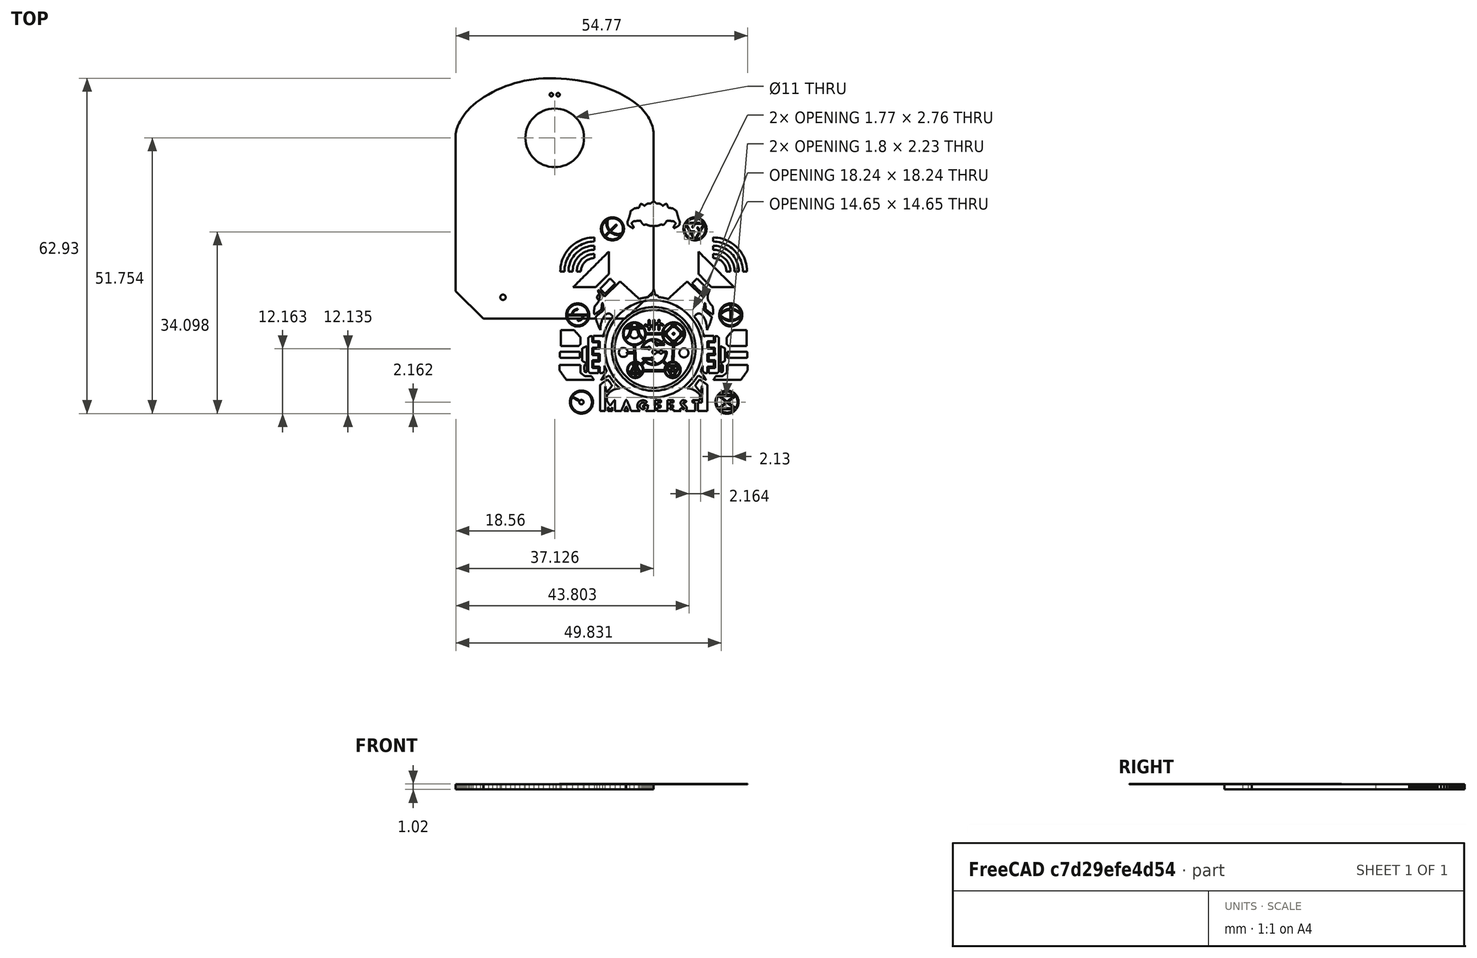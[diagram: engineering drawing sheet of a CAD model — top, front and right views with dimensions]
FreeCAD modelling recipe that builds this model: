
FCSTD DOCUMENT  (FreeCAD 0.19R24291 (Git))
Label: blade-plate-med-no-teeth
License: All rights reserved
LicenseURL: http://en.wikipedia.org/wiki/All_rights_reserved
objects: Part::Feature×106, Part::Extrusion×40, Part::MultiFuse×9, App::Part×5, PartDesign::CoordinateSystem×1, Sketcher::SketchObject×1
note: 157 computed .brp shape members not serialized (recipe doc carries the construction recipe); baked Part::Feature solids carry a one-line shape summary decoded from their .brp

FEATURE [PartDesign::CoordinateSystem] Local_CS_2f9
  AttacherType = Attacher::AttachEngine3D
FEATURE [Part::Feature] Pcb_2f9
  shape: bbox 37.12 x 45.09 x 1 mm, 78 faces (baked)
FEATURE [Sketcher::SketchObject] PCB_Sketch_2f9
  FullyConstrained = false
  sketch-geometry (72):
    g0: LineSegment StartX=18.2126 StartY=13.8473 StartZ=0 EndX=18.0682 EndY=14.2151 EndZ=0
    g1: LineSegment StartX=17.2906 StartY=15.6568 StartZ=0 EndX=17.0535 EndY=15.9973 EndZ=0
    g2: LineSegment StartX=17.7164 StartY=14.9469 StartZ=0 EndX=17.512 EndY=15.3058 EndZ=0
    g3: LineSegment StartX=18.4311 StartY=13.1203 StartZ=0 EndX=18.334 EndY=13.4816 EndZ=0
    g4: LineSegment StartX=17.9023 StartY=14.5825 StartZ=0 EndX=17.7164 EndY=14.9469 EndZ=0
    g5: LineSegment StartX=17.512 StartY=15.3058 StartZ=0 EndX=17.2906 EndY=15.6568 EndZ=0
    g6: LineSegment StartX=18.334 StartY=13.4816 StartZ=0 EndX=18.2126 EndY=13.8473 EndZ=0
    g7: LineSegment StartX=18.5022 StartY=12.7661 StartZ=0 EndX=18.4311 EndY=13.1203 EndZ=0
    g8: LineSegment StartX=18.0682 StartY=14.2151 StartZ=0 EndX=17.9023 EndY=14.5825 EndZ=0
    g9: LineSegment StartX=18.5609 StartY=12.0887 StartZ=0 EndX=18.546 EndY=12.4214 EndZ=0
    g10: LineSegment StartX=18.546 StartY=12.4214 StartZ=0 EndX=18.5022 EndY=12.7661 EndZ=0
    g11: LineSegment StartX=-1.00226 StartY=22.5449 StartZ=0 EndX=-2.16808 EndY=22.5134 EndZ=0
    g12: LineSegment StartX=-2.16808 StartY=22.5134 StartZ=0 EndX=-3.05347 EndY=22.4553 EndZ=0
    g13: LineSegment StartX=-3.05347 StartY=22.4553 StartZ=0 EndX=-3.94106 EndY=22.3603 EndZ=0
    g14: LineSegment StartX=-3.94106 StartY=22.3603 StartZ=0 EndX=-4.82869 EndY=22.2291 EndZ=0
    g15: LineSegment StartX=-4.82869 StartY=22.2291 StartZ=0 EndX=-5.71419 EndY=22.062 EndZ=0
    g16: LineSegment StartX=-5.71419 StartY=22.062 StartZ=0 EndX=-6.59539 EndY=21.8597 EndZ=0
    g17: LineSegment StartX=-6.59539 StartY=21.8597 StartZ=0 EndX=-7.47011 EndY=21.6227 EndZ=0
    g18: LineSegment StartX=-7.47011 StartY=21.6227 StartZ=0 EndX=-8.3362 EndY=21.3514 EndZ=0
    g19: LineSegment StartX=-8.3362 StartY=21.3514 StartZ=0 EndX=-9.19148 EndY=21.0464 EndZ=0
    g20: LineSegment StartX=-9.19148 StartY=21.0464 StartZ=0 EndX=-10.0338 EndY=20.7082 EndZ=0
    g21: LineSegment StartX=-10.0338 StartY=20.7082 StartZ=0 EndX=-10.8609 EndY=20.3374 EndZ=0
    g22: LineSegment StartX=-10.8609 StartY=20.3374 StartZ=0 EndX=-11.6708 EndY=19.9344 EndZ=0
    g23: LineSegment StartX=-11.6708 StartY=19.9344 StartZ=0 EndX=-12.4611 EndY=19.4999 EndZ=0
    g24: LineSegment StartX=-12.4611 StartY=19.4999 StartZ=0 EndX=-13.2298 EndY=19.0342 EndZ=0
    g25: LineSegment StartX=-13.2298 StartY=19.0342 StartZ=0 EndX=-13.9747 EndY=18.538 EndZ=0
    g26: LineSegment StartX=-13.9747 StartY=18.538 StartZ=0 EndX=-14.6936 EndY=18.0117 EndZ=0
    g27: LineSegment StartX=-14.6936 StartY=18.0117 StartZ=0 EndX=-15.3843 EndY=17.4559 EndZ=0
    g28: LineSegment StartX=-15.3843 StartY=17.4559 StartZ=0 EndX=-15.6818 EndY=17.19 EndZ=0
    g29: LineSegment StartX=-15.6818 StartY=17.19 StartZ=0 EndX=-15.9769 EndY=16.8978 EndZ=0
    g30: LineSegment StartX=-15.9769 StartY=16.8978 StartZ=0 EndX=-16.2674 EndY=16.5829 EndZ=0
    g31: LineSegment StartX=-16.2674 StartY=16.5829 StartZ=0 EndX=-16.5509 EndY=16.2489 EndZ=0
    g32: LineSegment StartX=-16.5509 StartY=16.2489 StartZ=0 EndX=-16.8251 EndY=15.8995 EndZ=0
    g33: LineSegment StartX=-16.8251 StartY=15.8995 StartZ=0 EndX=-17.0876 EndY=15.5384 EndZ=0
    g34: LineSegment StartX=-17.0876 StartY=15.5384 StartZ=0 EndX=-17.3361 EndY=15.1692 EndZ=0
    g35: LineSegment StartX=-17.3361 StartY=15.1692 StartZ=0 EndX=-17.5684 EndY=14.7956 EndZ=0
    g36: LineSegment StartX=-17.5684 StartY=14.7956 StartZ=0 EndX=-17.782 EndY=14.4213 EndZ=0
    g37: LineSegment StartX=-17.782 StartY=14.4213 StartZ=0 EndX=-17.9747 EndY=14.0499 EndZ=0
    g38: LineSegment StartX=-17.9747 StartY=14.0499 StartZ=0 EndX=-18.1441 EndY=13.6851 EndZ=0
    g39: LineSegment StartX=-18.1441 StartY=13.6851 StartZ=0 EndX=-18.2879 EndY=13.3306 EndZ=0
    g40: LineSegment StartX=-18.2879 StartY=13.3306 StartZ=0 EndX=-18.4039 EndY=12.9901 EndZ=0
    g41: LineSegment StartX=-18.4039 StartY=12.9901 StartZ=0 EndX=-18.4895 EndY=12.6671 EndZ=0
    g42: LineSegment StartX=-18.4895 StartY=12.6671 StartZ=0 EndX=-18.5426 EndY=12.3655 EndZ=0
    g43: LineSegment StartX=-18.5426 StartY=12.3655 StartZ=0 EndX=-18.5609 EndY=12.0887 EndZ=0
    g44: LineSegment StartX=-18.5609 StartY=12.0887 StartZ=0 EndX=-18.5609 EndY=-17.3932 EndZ=0
    g45: LineSegment StartX=-18.5609 StartY=-17.3932 StartZ=0 EndX=-13.4077 EndY=-22.5463 EndZ=0
    g46: LineSegment StartX=-13.4077 StartY=-22.5463 StartZ=0 EndX=13.4015 EndY=-22.5463 EndZ=0
    g47: LineSegment StartX=13.4015 StartY=-22.5463 StartZ=0 EndX=18.5609 EndY=-17.387 EndZ=0
    g48: LineSegment StartX=18.5609 StartY=-17.387 StartZ=0 EndX=18.5609 EndY=12.0887 EndZ=0
    g49: LineSegment StartX=17.0535 StartY=15.9973 StartZ=0 EndX=16.8024 EndY=16.3249 EndZ=0
    g50: LineSegment StartX=16.8024 StartY=16.3249 StartZ=0 EndX=16.5386 EndY=16.637 EndZ=0
    g51: LineSegment StartX=16.5386 StartY=16.637 StartZ=0 EndX=16.2636 EndY=16.9312 EndZ=0
    g52: LineSegment StartX=16.2636 StartY=16.9312 StartZ=0 EndX=15.979 EndY=17.205 EndZ=0
    g53: LineSegment StartX=15.979 StartY=17.205 StartZ=0 EndX=15.6861 EndY=17.4559 EndZ=0
    g54: LineSegment StartX=15.6861 StartY=17.4559 StartZ=0 EndX=14.8776 EndY=18.0704 EndZ=0
    g55: LineSegment StartX=14.8776 StartY=18.0704 StartZ=0 EndX=14.0352 EndY=18.6422 EndZ=0
    g56: LineSegment StartX=14.0352 StartY=18.6422 StartZ=0 EndX=13.1617 EndY=19.1719 EndZ=0
    g57: LineSegment StartX=13.1617 StartY=19.1719 StartZ=0 EndX=12.2595 EndY=19.6602 EndZ=0
    g58: LineSegment StartX=12.2595 StartY=19.6602 StartZ=0 EndX=11.3315 EndY=20.1077 EndZ=0
    g59: LineSegment StartX=11.3315 StartY=20.1077 StartZ=0 EndX=10.3802 EndY=20.5152 EndZ=0
    g60: LineSegment StartX=10.3802 StartY=20.5152 StartZ=0 EndX=9.40835 EndY=20.8832 EndZ=0
    g61: LineSegment StartX=9.40835 StartY=20.8832 StartZ=0 EndX=8.4186 EndY=21.2126 EndZ=0
    g62: LineSegment StartX=8.4186 StartY=21.2126 StartZ=0 EndX=7.41361 EndY=21.5039 EndZ=0
    g63: LineSegment StartX=7.41361 StartY=21.5039 StartZ=0 EndX=6.39603 EndY=21.7579 EndZ=0
    g64: LineSegment StartX=6.39603 StartY=21.7579 StartZ=0 EndX=5.36853 EndY=21.9751 EndZ=0
    g65: LineSegment StartX=5.36853 StartY=21.9751 StartZ=0 EndX=4.33378 EndY=22.1563 EndZ=0
    g66: LineSegment StartX=4.33378 StartY=22.1563 StartZ=0 EndX=3.29443 EndY=22.3022 EndZ=0
    g67: LineSegment StartX=3.29443 StartY=22.3022 StartZ=0 EndX=2.25315 EndY=22.4135 EndZ=0
    g68: LineSegment StartX=2.25315 StartY=22.4135 StartZ=0 EndX=1.2126 EndY=22.4907 EndZ=0
    g69: LineSegment StartX=1.2126 StartY=22.4907 StartZ=0 EndX=0.175441 EndY=22.5346 EndZ=0
    g70: LineSegment StartX=0.175441 StartY=22.5346 StartZ=0 EndX=-1.00226 EndY=22.5449 EndZ=0
    g71: Circle CenterX=0 CenterY=11.3637 CenterZ=0 NormalX=0 NormalY=0 NormalZ=1 AngleXU=0 Radius=5.5
  constraints (71):
    c: Coincident(g45,g44)
    c: Coincident(g43,g44)
    c: Coincident(g43,g42)
    c: Coincident(g42,g41)
    c: Coincident(g41,g40)
    c: Coincident(g40,g39)
    c: Coincident(g39,g38)
    c: Coincident(g38,g37)
    c: Coincident(g37,g36)
    c: Coincident(g36,g35)
    c: Coincident(g35,g34)
    c: Coincident(g34,g33)
    c: Coincident(g32,g33)
    c: Coincident(g32,g31)
    c: Coincident(g30,g31)
    c: Coincident(g29,g30)
    c: Coincident(g28,g29)
    c: Coincident(g27,g28)
    c: Coincident(g27,g26)
    c: Coincident(g25,g26)
    c: Coincident(g46,g45)
    c: Coincident(g24,g25)
    c: Coincident(g24,g23)
    c: Coincident(g23,g22)
    c: Coincident(g22,g21)
    c: Coincident(g20,g21)
    c: Coincident(g19,g20)
    c: Coincident(g18,g19)
    c: Coincident(g17,g18)
    c: Coincident(g17,g16)
    c: Coincident(g16,g15)
    c: Coincident(g15,g14)
    c: Coincident(g14,g13)
    c: Coincident(g13,g12)
    c: Coincident(g12,g11)
    c: Coincident(g11,g70)
    c: Coincident(g70,g69)
    c: Coincident(g68,g69)
    c: Coincident(g67,g68)
    c: Coincident(g66,g67)
    c: Coincident(g65,g66)
    c: Coincident(g65,g64)
    c: Coincident(g63,g64)
    c: Coincident(g62,g63)
    c: Coincident(g62,g61)
    c: Coincident(g60,g61)
    c: Coincident(g60,g59)
    c: Coincident(g59,g58)
    c: Coincident(g58,g57)
    c: Coincident(g56,g57)
    c: Coincident(g46,g47)
    c: Coincident(g55,g56)
    c: Coincident(g55,g54)
    c: Coincident(g54,g53)
    c: Coincident(g52,g53)
    c: Coincident(g51,g52)
    c: Coincident(g51,g50)
    c: Coincident(g49,g50)
    c: Coincident(g1,g49)
    c: Coincident(g1,g5)
    c: Coincident(g5,g2)
    c: Coincident(g4,g2)
    c: Coincident(g8,g4)
    c: Coincident(g0,g8)
    c: Coincident(g0,g6)
    c: Coincident(g6,g3)
    c: Coincident(g3,g7)
    c: Coincident(g10,g7)
    c: Coincident(g10,g9)
    c: Coincident(g48,g47)
    c: Coincident(g48,g9)
FEATURE [App::Part] Board_Geoms_2f9
  Group = -> [Local_CS_2f9,Pcb_2f9,PCB_Sketch_2f9]
  Origin = -> Origin
FEATURE [App::Part] Step_Models_2f9
  Origin = -> Origin002
FEATURE [App::Part] Board_2f9  label="blade-plate-med-no-teeth"
  Group = -> [Board_Geoms_2f9,Step_Models_2f9]
  Origin = -> Origin001
FEATURE [Part::Feature] path950
  shape: bbox 6.431 x 2.806 x 2e-07 mm, 0 faces, 0 solids (baked)
FEATURE [Part::Feature] path952
  shape: bbox 2.242 x 5.916 x 2e-07 mm, 0 faces, 0 solids (baked)
FEATURE [Part::Feature] path948
  shape: bbox 6.431 x 2.806 x 2e-07 mm, 0 faces, 0 solids (baked)
FEATURE [Part::Feature] path946
  shape: bbox 0.4955 x 1.452 x 2e-07 mm, 0 faces, 0 solids (baked)
FEATURE [Part::Feature] path942
  shape: bbox 3.739 x 1.126 x 2e-07 mm, 0 faces, 0 solids (baked)
FEATURE [Part::Feature] path938
  shape: bbox 0.8516 x 3.223 x 2e-07 mm, 0 faces, 0 solids (baked)
FEATURE [Part::Feature] path936
  shape: bbox 0.8516 x 3.223 x 2e-07 mm, 0 faces, 0 solids (baked)
FEATURE [Part::Feature] path934
  shape: bbox 1.909 x 6.981 x 2e-07 mm, 0 faces, 0 solids (baked)
FEATURE [Part::Feature] path932
  shape: bbox 1.909 x 6.981 x 2e-07 mm, 0 faces, 0 solids (baked)
FEATURE [Part::Feature] path940
  shape: bbox 3.739 x 1.126 x 2e-07 mm, 0 faces, 0 solids (baked)
FEATURE [Part::Feature] path930
  shape: bbox 3.738 x 2.965 x 2e-07 mm, 0 faces, 0 solids (baked)
FEATURE [Part::Feature] path928
  shape: bbox 3.738 x 2.965 x 2e-07 mm, 0 faces, 0 solids (baked)
FEATURE [Part::Feature] path944
  shape: bbox 0.4954 x 1.452 x 2e-07 mm, 0 faces, 0 solids (baked)
FEATURE [Part::Feature] path954
  shape: bbox 2.232 x 5.914 x 2e-07 mm, 0 faces, 0 solids (baked)
FEATURE [Part::Feature] path958
  shape: bbox 0.8191 x 0.724 x 2e-07 mm, 0 faces, 0 solids (baked)
FEATURE [Part::Feature] path956
  shape: bbox 0.8346 x 0.8904 x 2e-07 mm, 0 faces, 0 solids (baked)
FEATURE [Part::Feature] path926
  shape: bbox 14.65 x 14.65 x 2e-07 mm, 0 faces, 0 solids (baked)
FEATURE [Part::Feature] path920
  shape: bbox 2.839 x 2.838 x 2e-07 mm, 0 faces, 0 solids (baked)
FEATURE [Part::Feature] path904
  shape: bbox 6.368 x 6.368 x 2e-07 mm, 0 faces, 0 solids (baked)
FEATURE [Part::Feature] path906
  shape: bbox 4.82 x 4.82 x 2e-07 mm, 0 faces, 0 solids (baked)
FEATURE [Part::Feature] path918
  shape: bbox 2.838 x 2.838 x 2e-07 mm, 0 faces, 0 solids (baked)
FEATURE [Part::Feature] path924
  shape: bbox 18.24 x 18.24 x 2e-07 mm, 0 faces, 0 solids (baked)
FEATURE [Part::Feature] path908
  shape: bbox 4.82 x 4.82 x 2e-07 mm, 0 faces, 0 solids (baked)
FEATURE [Part::Feature] path916
  shape: bbox 3.272 x 3.272 x 2e-07 mm, 0 faces, 0 solids (baked)
FEATURE [Part::Feature] path912
  shape: bbox 6.702 x 6.691 x 2e-07 mm, 0 faces, 0 solids (baked)
FEATURE [Part::Feature] path857_8_0_9
  shape: bbox 9.846 x 4.976 x 2e-07 mm, 0 faces, 0 solids (baked)
FEATURE [Part::Feature] path914
  shape: bbox 3.272 x 3.272 x 2e-07 mm, 0 faces, 0 solids (baked)
FEATURE [Part::Feature] path902
  shape: bbox 6.368 x 6.368 x 2e-07 mm, 0 faces, 0 solids (baked)
FEATURE [Part::Feature] path922
  shape: bbox 22.57 x 24.3 x 2e-07 mm, 0 faces, 0 solids (baked)
FEATURE [Part::MultiFuse] Fusion
  Shapes = -> [path924,path922]
FEATURE [Part::Feature] path910
  shape: bbox 6.702 x 6.691 x 2e-07 mm, 0 faces, 0 solids (baked)
FEATURE [Part::Extrusion] Extrude036
  Base = -> path944
  Dir = (0,0,1)
  DirMode = 0
  FaceMakerClass = Part::FaceMakerBullseye
  LengthFwd = 0.01
  LengthRev = 0
  Solid = true
  Symmetric = false
FEATURE [Part::Extrusion] Extrude039
  Base = -> path938
  Dir = (0,0,1)
  DirMode = 0
  FaceMakerClass = Part::FaceMakerBullseye
  LengthFwd = 0.01
  LengthRev = 0
  Solid = true
  Symmetric = false
FEATURE [Part::Extrusion] Extrude041
  Base = -> path934
  Dir = (0,0,1)
  DirMode = 0
  FaceMakerClass = Part::FaceMakerBullseye
  LengthFwd = 0.01
  LengthRev = 0
  Solid = true
  Symmetric = false
FEATURE [Part::Extrusion] Extrude042
  Base = -> path932
  Dir = (0,0,1)
  DirMode = 0
  FaceMakerClass = Part::FaceMakerBullseye
  LengthFwd = 0.01
  LengthRev = 0
  Solid = true
  Symmetric = false
FEATURE [Part::Extrusion] Extrude040
  Base = -> path936
  Dir = (0,0,1)
  DirMode = 0
  FaceMakerClass = Part::FaceMakerBullseye
  LengthFwd = 0.01
  LengthRev = 0
  Solid = true
  Symmetric = false
FEATURE [Part::Extrusion] Extrude043
  Base = -> path930
  Dir = (0,0,1)
  DirMode = 0
  FaceMakerClass = Part::FaceMakerBullseye
  LengthFwd = 0.01
  LengthRev = 0
  Solid = true
  Symmetric = false
FEATURE [Part::Extrusion] Extrude029
  Base = -> path958
  Dir = (0,0,1)
  DirMode = 0
  FaceMakerClass = Part::FaceMakerBullseye
  LengthFwd = 0.01
  LengthRev = 0
  Solid = true
  Symmetric = false
FEATURE [Part::Extrusion] Extrude030
  Base = -> path956
  Dir = (0,0,1)
  DirMode = 0
  FaceMakerClass = Part::FaceMakerBullseye
  LengthFwd = 0.01
  LengthRev = 0
  Solid = true
  Symmetric = false
FEATURE [Part::Extrusion] Extrude034
  Base = -> path948
  Dir = (0,0,1)
  DirMode = 0
  FaceMakerClass = Part::FaceMakerBullseye
  LengthFwd = 0.01
  LengthRev = 0
  Solid = true
  Symmetric = false
FEATURE [Part::Extrusion] Extrude035
  Base = -> path946
  Dir = (0,0,1)
  DirMode = 0
  FaceMakerClass = Part::FaceMakerBullseye
  LengthFwd = 0.01
  LengthRev = 0
  Solid = true
  Symmetric = false
FEATURE [Part::Extrusion] Extrude038
  Base = -> path940
  Dir = (0,0,1)
  DirMode = 0
  FaceMakerClass = Part::FaceMakerBullseye
  LengthFwd = 0.01
  LengthRev = 0
  Solid = true
  Symmetric = false
FEATURE [Part::Extrusion] Extrude032
  Base = -> path952
  Dir = (0,0,1)
  DirMode = 0
  FaceMakerClass = Part::FaceMakerBullseye
  LengthFwd = 0.01
  LengthRev = 0
  Solid = true
  Symmetric = false
FEATURE [Part::Extrusion] Extrude066
  Base = -> path942
  Dir = (0,0,1)
  DirMode = 0
  FaceMakerClass = Part::FaceMakerBullseye
  LengthFwd = 0.01
  LengthRev = 0
  Solid = true
  Symmetric = false
FEATURE [Part::Extrusion] Extrude046
  Base = -> path920
  Dir = (0,0,1)
  DirMode = 0
  FaceMakerClass = Part::FaceMakerBullseye
  LengthFwd = 0.01
  LengthRev = 0
  Solid = true
  Symmetric = false
FEATURE [Part::Extrusion] Extrude062
  Base = -> path950
  Dir = (0,0,1)
  DirMode = 0
  FaceMakerClass = Part::FaceMakerBullseye
  LengthFwd = 0.01
  LengthRev = 0
  Solid = true
  Symmetric = false
FEATURE [Part::Extrusion] Extrude076
  Base = -> path918
  Dir = (0,0,1)
  DirMode = 0
  FaceMakerClass = Part::FaceMakerBullseye
  LengthFwd = 0.01
  LengthRev = 0
  Solid = true
  Symmetric = false
FEATURE [Part::Extrusion] Extrude050
  Base = -> path912
  Dir = (0,0,1)
  DirMode = 0
  FaceMakerClass = Part::FaceMakerBullseye
  LengthFwd = 0.01
  LengthRev = 0
  Solid = true
  Symmetric = false
FEATURE [Part::Extrusion] Extrude048
  Base = -> path916
  Dir = (0,0,1)
  DirMode = 0
  FaceMakerClass = Part::FaceMakerBullseye
  LengthFwd = 0.01
  LengthRev = 0
  Solid = true
  Symmetric = false
FEATURE [Part::Extrusion] Extrude045
  Base = -> path926
  Dir = (0,0,1)
  DirMode = 0
  FaceMakerClass = Part::FaceMakerBullseye
  LengthFwd = 0.01
  LengthRev = 0
  Solid = true
  Symmetric = false
FEATURE [Part::Extrusion] Extrude049
  Base = -> path914
  Dir = (0,0,1)
  DirMode = 0
  FaceMakerClass = Part::FaceMakerBullseye
  LengthFwd = 0.01
  LengthRev = 0
  Solid = true
  Symmetric = false
FEATURE [Part::Extrusion] Extrude051
  Base = -> path910
  Dir = (0,0,1)
  DirMode = 0
  FaceMakerClass = Part::FaceMakerBullseye
  LengthFwd = 0.01
  LengthRev = 0
  Solid = true
  Symmetric = false
FEATURE [Part::Extrusion] Extrude053
  Base = -> path906
  Dir = (0,0,1)
  DirMode = 0
  FaceMakerClass = Part::FaceMakerBullseye
  LengthFwd = 0.01
  LengthRev = 0
  Solid = true
  Symmetric = false
FEATURE [Part::Extrusion] Extrude055
  Base = -> path902
  Dir = (0,0,1)
  DirMode = 0
  FaceMakerClass = Part::FaceMakerBullseye
  LengthFwd = 0.01
  LengthRev = 0
  Solid = true
  Symmetric = false
FEATURE [Part::Extrusion] Extrude056
  Base = -> path857_8_0_9
  Dir = (0,0,1)
  DirMode = 0
  FaceMakerClass = Part::FaceMakerBullseye
  LengthFwd = 0.01
  LengthRev = 0
  Solid = true
  Symmetric = false
FEATURE [Part::Extrusion] Extrude057
  Base = -> Fusion
  Dir = (0,0,1)
  DirMode = 0
  FaceMakerClass = Part::FaceMakerBullseye
  LengthFwd = 0.01
  LengthRev = 0
  Solid = true
  Symmetric = false
FEATURE [Part::Extrusion] Extrude044
  Base = -> path928
  Dir = (0,0,1)
  DirMode = 0
  FaceMakerClass = Part::FaceMakerBullseye
  LengthFwd = 0.01
  LengthRev = 0
  Solid = true
  Symmetric = false
FEATURE [Part::Extrusion] Extrude083
  Base = -> path904
  Dir = (0,0,1)
  DirMode = 0
  FaceMakerClass = Part::FaceMakerBullseye
  LengthFwd = 0.01
  LengthRev = 0
  Solid = true
  Symmetric = false
FEATURE [Part::Extrusion] Extrude081
  Base = -> path908
  Dir = (0,0,1)
  DirMode = 0
  FaceMakerClass = Part::FaceMakerBullseye
  LengthFwd = 0.01
  LengthRev = 0
  Solid = true
  Symmetric = false
FEATURE [Part::Feature] path7669_6_9_7_1_4
  shape: bbox 4.579 x 2.816 x 2e-07 mm, 1 faces, 0 solids (baked)
FEATURE [Part::Feature] path959_74_5_9
  shape: bbox 1.157 x 1.157 x 2e-07 mm, 1 faces, 0 solids (baked)
FEATURE [Part::Feature] path1142_5_3
  shape: bbox 1.86 x 1.86 x 2e-07 mm, 1 faces, 0 solids (baked)
FEATURE [Part::Feature] path1139_8_8
  shape: bbox 1.86 x 1.86 x 2e-07 mm, 1 faces, 0 solids (baked)
FEATURE [Part::Feature] path959_7_3_0_1
  shape: bbox 1.157 x 1.157 x 2e-07 mm, 1 faces, 0 solids (baked)
FEATURE [Part::Feature] path959_7_34_5
  shape: bbox 1.157 x 1.157 x 2e-07 mm, 1 faces, 0 solids (baked)
FEATURE [Part::Feature] rect1059_6_6
  shape: bbox 1.86 x 1.86 x 2e-07 mm, 1 faces, 0 solids (baked)
FEATURE [Part::Feature] rect1081_4_5_7
  shape: bbox 2.152 x 4.303 x 2e-07 mm, 1 faces, 0 solids (baked)
FEATURE [Part::Feature] rect1081_5_0_2
  shape: bbox 2.152 x 4.303 x 2e-07 mm, 1 faces, 0 solids (baked)
FEATURE [Part::Feature] rect1081_4_0_1_9
  shape: bbox 2.152 x 4.303 x 2e-07 mm, 1 faces, 0 solids (baked)
FEATURE [Part::Feature] path1849_7_9
  Placement = pos=(-72.7848,130.054,0) rot=(0,0,1;0rad)
  shape: bbox 1.711 x 1.711 x 2e-07 mm, 1 faces, 0 solids (baked)
FEATURE [Part::Feature] rect1857_9_3
  shape: bbox 3.613 x 0.2543 x 2e-07 mm, 1 faces, 0 solids (baked)
FEATURE [Part::Feature] path959_3_7
  shape: bbox 1.157 x 1.157 x 2e-07 mm, 1 faces, 0 solids (baked)
FEATURE [Part::Feature] rect1081_3_2
  shape: bbox 2.152 x 4.303 x 2e-07 mm, 1 faces, 0 solids (baked)
FEATURE [Part::Feature] path1108_9_5
  shape: bbox 1.86 x 1.86 x 2e-07 mm, 1 faces, 0 solids (baked)
FEATURE [Part::Feature] path7669_6_9_6_5
  shape: bbox 4.395 x 1.945 x 2e-07 mm, 1 faces, 0 solids (baked)
FEATURE [Part::Feature] path1387
  shape: bbox 2.857 x 0.6324 x 2e-07 mm, 0 faces, 0 solids (baked)
FEATURE [Part::Feature] path1401
  shape: bbox 3.191 x 0.8343 x 2e-07 mm, 0 faces, 0 solids (baked)
FEATURE [Part::Feature] path1415
  shape: bbox 2.983 x 1.481 x 2e-07 mm, 0 faces, 0 solids (baked)
FEATURE [Part::Feature] path1265
  shape: bbox 4.525 x 4.463 x 2e-07 mm, 0 faces, 0 solids (baked)
FEATURE [Part::Feature] path1405
  shape: bbox 1.856 x 2.763 x 2e-07 mm, 0 faces, 0 solids (baked)
FEATURE [Part::Feature] path1297
  shape: bbox 4.563 x 4.468 x 2e-07 mm, 0 faces, 0 solids (baked)
FEATURE [Part::Feature] path1407
  shape: bbox 1.805 x 2.762 x 2e-07 mm, 0 faces, 0 solids (baked)
FEATURE [Part::Feature] path1403
  shape: bbox 3.293 x 2.849 x 2e-07 mm, 0 faces, 0 solids (baked)
FEATURE [Part::Feature] path1253
  shape: bbox 4.564 x 4.449 x 2e-07 mm, 0 faces, 0 solids (baked)
FEATURE [Part::Feature] path1413
  shape: bbox 1.481 x 2.981 x 2e-07 mm, 0 faces, 0 solids (baked)
FEATURE [Part::Feature] path1411
  shape: bbox 3.034 x 2.972 x 2e-07 mm, 0 faces, 0 solids (baked)
FEATURE [Part::Feature] path1389
  shape: bbox 2.672 x 1.025 x 2e-07 mm, 0 faces, 0 solids (baked)
FEATURE [Part::Feature] rect1270_8_2_80
  shape: bbox 0.4357 x 3.344 x 2e-07 mm, 1 faces, 0 solids (baked)
FEATURE [Part::Feature] path2766_2_6
  shape: bbox 1.318 x 2.285 x 2e-07 mm, 1 faces, 0 solids (baked)
FEATURE [Part::Feature] path2577_5_9
  shape: bbox 1.312 x 2.285 x 2e-07 mm, 1 faces, 0 solids (baked)
FEATURE [Part::Feature] path2376_2_1_7_1_5_5
  shape: bbox 0.9033 x 0.9033 x 2e-07 mm, 1 faces, 0 solids (baked)
FEATURE [Part::Feature] path2536_4_8_8
  shape: bbox 0.5554 x 0.5554 x 2e-07 mm, 1 faces, 0 solids (baked)
FEATURE [Part::Feature] path2536_7_2_0
  shape: bbox 0.5554 x 0.5554 x 2e-07 mm, 1 faces, 0 solids (baked)
FEATURE [Part::Feature] rect1270_3
  shape: bbox 3.165 x 0.2677 x 2e-07 mm, 1 faces, 0 solids (baked)
FEATURE [Part::Feature] rect1270_8_2_8_0
  shape: bbox 0.4357 x 3.344 x 2e-07 mm, 1 faces, 0 solids (baked)
FEATURE [Part::Feature] path2376_0
  shape: bbox 1.713 x 1.713 x 2e-07 mm, 0 faces, 0 solids (baked)
FEATURE [Part::Extrusion] Extrude088
  Base = -> path2376_0
  Dir = (0,0,1)
  DirMode = 0
  FaceMakerClass = Part::FaceMakerBullseye
  LengthFwd = 0.02
  LengthRev = 0
  Solid = true
  Symmetric = false
FEATURE [Part::Feature] rect2443_9_0
  shape: bbox 0.1757 x 2.045 x 2e-07 mm, 1 faces, 0 solids (baked)
FEATURE [Part::Feature] path1277
  shape: bbox 4.563 x 4.468 x 2e-07 mm, 0 faces, 0 solids (baked)
FEATURE [Part::Feature] path2536_8_1
  shape: bbox 0.5554 x 0.5554 x 2e-07 mm, 1 faces, 0 solids (baked)
FEATURE [Part::Feature] path1489_8_2
  shape: bbox 0.942 x 0.942 x 2e-07 mm, 1 faces, 0 solids (baked)
FEATURE [Part::Feature] path1875_9_6
  shape: bbox 1.46 x 3.14 x 2e-07 mm, 1 faces, 0 solids (baked)
FEATURE [Part::Feature] path1875_0_1_3
  shape: bbox 1.46 x 3.14 x 2e-07 mm, 1 faces, 0 solids (baked)
FEATURE [Part::Feature] path2088_1_1_1
  shape: bbox 1.531 x 3.062 x 2e-07 mm, 1 faces, 0 solids (baked)
FEATURE [Part::Feature] path2118_4_2_1
  shape: bbox 1.532 x 3.062 x 2e-07 mm, 1 faces, 0 solids (baked)
FEATURE [Part::Feature] rect1270_8_5_2
  shape: bbox 1.5 x 0.2677 x 2e-07 mm, 1 faces, 0 solids (baked)
FEATURE [Part::Feature] path1377
  shape: bbox 3.891 x 1.793 x 2e-07 mm, 0 faces, 0 solids (baked)
FEATURE [Part::Feature] path1371
  shape: bbox 1.847 x 1.688 x 2e-07 mm, 0 faces, 0 solids (baked)
FEATURE [Part::Feature] path2376_2_1_6_8_8
  Placement = pos=(-74.8536,126.557,0) rot=(0,0,1;0rad)
  shape: bbox 1.713 x 1.713 x 2e-07 mm, 1 faces, 0 solids (baked)
FEATURE [Part::Feature] path8031_8
  shape: bbox 3.53 x 1.981 x 2e-07 mm, 0 faces, 0 solids (baked)
FEATURE [Part::Extrusion] Extrude091
  Base = -> path8031_8
  Dir = (0,0,1)
  DirMode = 0
  FaceMakerClass = Part::FaceMakerBullseye
  LengthFwd = 0.02
  LengthRev = 0
  Solid = true
  Symmetric = false
FEATURE [Part::Feature] path1383
  shape: bbox 3.925 x 1.972 x 2e-07 mm, 0 faces, 0 solids (baked)
FEATURE [Part::Feature] path2376_2_1_7_1_48_8_4_2
  shape: bbox 0.7776 x 0.7776 x 2e-07 mm, 1 faces, 0 solids (baked)
FEATURE [Part::Feature] path10299_4
  shape: bbox 0.3689 x 0.3694 x 2e-07 mm, 0 faces, 0 solids (baked)
FEATURE [Part::Extrusion] Extrude089
  Base = -> path10299_4
  Dir = (0,0,1)
  DirMode = 0
  FaceMakerClass = Part::FaceMakerBullseye
  LengthFwd = 0.02
  LengthRev = 0
  Solid = true
  Symmetric = false
FEATURE [Part::Feature] path1381
  shape: bbox 3.926 x 1.869 x 2e-07 mm, 0 faces, 0 solids (baked)
FEATURE [Part::Feature] path2376_2_1_7_1_48_89_5
  shape: bbox 0.7776 x 0.7776 x 2e-07 mm, 1 faces, 0 solids (baked)
FEATURE [Part::Feature] path1369
  shape: bbox 1.846 x 1.684 x 2e-07 mm, 0 faces, 0 solids (baked)
FEATURE [Part::Feature] path1489_6
  shape: bbox 0.942 x 0.942 x 2e-07 mm, 1 faces, 0 solids (baked)
FEATURE [Part::Feature] path1373
  shape: bbox 1.836 x 1.915 x 2e-07 mm, 0 faces, 0 solids (baked)
FEATURE [Part::Feature] rect1270_8_6
  shape: bbox 4.112 x 0.2677 x 2e-07 mm, 1 faces, 0 solids (baked)
FEATURE [Part::Feature] path1273
  shape: bbox 4.563 x 4.468 x 2e-07 mm, 0 faces, 0 solids (baked)
FEATURE [Part::Feature] path1269
  shape: bbox 4.563 x 4.451 x 2e-07 mm, 0 faces, 0 solids (baked)
FEATURE [Part::Feature] path2118_5_5_5
  shape: bbox 1.532 x 3.062 x 2e-07 mm, 1 faces, 0 solids (baked)
FEATURE [Part::Feature] path1397
  shape: bbox 2.871 x 0.6613 x 2e-07 mm, 0 faces, 0 solids (baked)
FEATURE [Part::Feature] path1395
  shape: bbox 2.655 x 1.019 x 2e-07 mm, 0 faces, 0 solids (baked)
FEATURE [Part::Feature] path1393
  shape: bbox 1.826 x 2.23 x 2e-07 mm, 0 faces, 0 solids (baked)
FEATURE [Part::Feature] path1391
  shape: bbox 1.826 x 2.231 x 2e-07 mm, 0 faces, 0 solids (baked)
FEATURE [Part::Feature] path1375
  shape: bbox 1.832 x 1.915 x 2e-07 mm, 0 faces, 0 solids (baked)
FEATURE [Part::Feature] path1365
  shape: bbox 4.136 x 4.058 x 2e-07 mm, 0 faces, 0 solids (baked)
FEATURE [Part::Feature] path2088_9_5_6
  shape: bbox 1.531 x 3.062 x 2e-07 mm, 1 faces, 0 solids (baked)
FEATURE [Part::Feature] path2182_0_4_3_8
  shape: bbox 1.211 x 2.1 x 2e-07 mm, 1 faces, 0 solids (baked)
FEATURE [Part::Feature] path2182_0_0_8
  shape: bbox 1.211 x 2.1 x 2e-07 mm, 1 faces, 0 solids (baked)
FEATURE [Part::Feature] rect1392_7_6_1
  shape: bbox 0.7492 x 0.7492 x 2e-07 mm, 1 faces, 0 solids (baked)
FEATURE [Part::Feature] rect1392_7_4
  shape: bbox 0.7492 x 0.7492 x 2e-07 mm, 1 faces, 0 solids (baked)
FEATURE [Part::Feature] path1427
  shape: bbox 14.65 x 14.65 x 2e-07 mm, 0 faces, 0 solids (baked)
FEATURE [Part::Feature] path8265_3
  shape: bbox 15.74 x 15.74 x 2e-07 mm, 0 faces, 0 solids (baked)
FEATURE [Part::MultiFuse] Fusion001
  Shapes = -> [path1365,path1277]
FEATURE [Part::Extrusion] Extrude087
  Base = -> Fusion001
  Dir = (0,0,1)
  DirMode = 0
  FaceMakerClass = Part::FaceMakerBullseye
  LengthFwd = 0.02
  LengthRev = 0
  Solid = true
  Symmetric = false
FEATURE [Part::MultiFuse] Fusion002
  Shapes = -> [path1383,path1381,path1269]
FEATURE [Part::Extrusion] Extrude090
  Base = -> Fusion002
  Dir = (0,0,1)
  DirMode = 0
  FaceMakerClass = Part::FaceMakerBullseye
  LengthFwd = 0.02
  LengthRev = 0
  Solid = true
  Symmetric = false
FEATURE [Part::MultiFuse] Fusion003
  Shapes = -> [path1415,path1413,path1411,path1253]
FEATURE [Part::MultiFuse] Fusion004
  Shapes = -> [path1407,path1405,path1403,path1401,path1297]
FEATURE [Part::MultiFuse] Fusion005
  Shapes = -> [path1377,path1375,path1373,path1371,path1369,path1273]
FEATURE [Part::MultiFuse] Fusion006
  Shapes = -> [path1397,path1395,path1393,path1391,path1389,path1387,path1265]
FEATURE [Part::MultiFuse] Fusion007
  Shapes = -> [path8265_3,path1427]
FEATURE [Part::MultiFuse] Fusion008
  Shapes = -> [path7669_6_9_6_5,path7669_6_9_7_1_4,path959_3_7,path959_7_34_5,path959_74_5_9,path959_7_3_0_1,path1142_5_3,path1108_9_5,path1139_8_8,rect1059_6_6,rect1081_3_2,rect1081_4_5_7,rect1081_5_0_2,rect1081_4_0_1_9,path1849_7_9,rect1857_9_3,path1875_9_6,path1875_0_1_3,path2118_4_2_1,path2088_9_5_6,path2182_0_0_8,path2376_2_1_7_1_5_5,path2376_2_1_7_1_48_89_5,path2376_2_1_7_1_48_8_4_2,rect2443_9_0,+18 more]
FEATURE [Part::Extrusion] Extrude092
  Base = -> Fusion008
  Dir = (0,0,1)
  DirMode = 0
  FaceMakerClass = Part::FaceMakerBullseye
  LengthFwd = 0.02
  LengthRev = 0
  Solid = true
  Symmetric = false
FEATURE [Part::Extrusion] Extrude103
  Base = -> Fusion007
  Dir = (0,0,1)
  DirMode = 0
  FaceMakerClass = Part::FaceMakerBullseye
  LengthFwd = 0.02
  LengthRev = 0
  Solid = true
  Symmetric = false
FEATURE [Part::Extrusion] Extrude105
  Base = -> Fusion004
  Dir = (0,0,1)
  DirMode = 0
  FaceMakerClass = Part::FaceMakerBullseye
  LengthFwd = 0.02
  LengthRev = 0
  Solid = true
  Symmetric = false
FEATURE [Part::Extrusion] Extrude106
  Base = -> Fusion005
  Dir = (0,0,1)
  DirMode = 0
  FaceMakerClass = Part::FaceMakerBullseye
  LengthFwd = 0.02
  LengthRev = 0
  Solid = true
  Symmetric = false
FEATURE [Part::Extrusion] Extrude107
  Base = -> Fusion006
  Dir = (0,0,1)
  DirMode = 0
  FaceMakerClass = Part::FaceMakerBullseye
  LengthFwd = 0.02
  LengthRev = 0
  Solid = true
  Symmetric = false
FEATURE [Part::Extrusion] Extrude108
  Base = -> Fusion003
  Dir = (0,0,1)
  DirMode = 0
  FaceMakerClass = Part::FaceMakerBullseye
  LengthFwd = 0.02
  LengthRev = 0
  Solid = true
  Symmetric = false
FEATURE [App::Part] Part001
  Group = -> [Extrude088,path2376_0,Extrude091,path8031_8,Extrude089,path10299_4,Extrude087,path1277,path1365,Fusion001,Extrude090,path1383,path1381,path1269,Fusion002,path1415,path1253,path1413,path1411,Fusion003,Extrude108,path1401,path1405,path1297,path1407,path1403,Fusion004,Extrude105,path1377,path1371,path1369,path1373,path1273,path1375,Fusion005,Extrude106,path1387,path1265,path1389,path1397,path1395,+53 more]
  Origin = -> Origin004
  Placement = pos=(-18.5,22.5,0) rot=(0,0,1;0rad)
FEATURE [Part::Extrusion] Extrude031
  Base = -> path954
  Dir = (0,0,1)
  DirMode = 0
  FaceMakerClass = Part::FaceMakerBullseye
  LengthFwd = 0.01
  LengthRev = 0
  Solid = true
  Symmetric = false
FEATURE [App::Part] Part
  Group = -> [path958,Extrude029,path956,Extrude030,path954,Extrude031,path952,Extrude032,path950,Extrude062,path948,Extrude034,path946,Extrude035,path944,Extrude036,path942,Extrude066,path940,Extrude038,path938,Extrude039,path936,Extrude040,path934,Extrude041,path932,Extrude042,path930,Extrude043,path928,Extrude044,path926,Extrude045,path920,Extrude046,path918,Extrude076,path916,Extrude048,path914,Extrude049,+18 more]
  Origin = -> Origin003
  Placement = pos=(-18.5,22.5,0) rot=(0,0,1;0rad)
